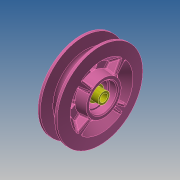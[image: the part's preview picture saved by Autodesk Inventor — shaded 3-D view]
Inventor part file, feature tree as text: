
AUTODESK INVENTOR PART (.ipt)
format: ipt  version: 2017 (Build 210142000, 142)  size: 988,160 bytes
history: native  units: mm
features: sketch x5, revolve x4, extrude x3, other x2, chamfer x2, plane x2, fillet x1, pattern_circular x1, projected_geometry x1
ambient origin geometry x8: Origin, YZ Plane, XZ Plane, XY Plane, X Axis, Y Axis, Z Axis, Center Point
bodies: Body1 (feature_tree), Body2 (feature_tree)
feature tree (21):
  other  "Sólido1"
  sketch  "Boceto1"  dims[d0=8.0mm d1=28.5mm]
  revolve  "Revolución1"  [1 undecoded]
  sketch  "Boceto2"  dims[d2=24.5mm d3=6.0mm]
  extrude  "Extrusión1"  Depth=6.0mm
  chamfer  "Chaflán1"  Distance=20.0mm
  extrude  "Extrusión2"  Depth=1.0mm
  extrude  "Extrusión3"  Depth=8.0mm
  chamfer  "Chaflán2"  Distance=3.0mm
  plane  "Plano de trabajo1"
  revolve  "Revolución3"  [1 undecoded]
  fillet  "Empalme1"  Radius=48.0mm
  plane  "Plano de trabajo2"
  revolve  "Revolución4"  [1 undecoded]
  pattern_circular  "Patrón circular1"  [2 undecoded]
  revolve  "Revolución2"  [1 undecoded]
  other  "espaciador"
  sketch  "Boceto3"  dims[d4=4.0mm]
  sketch  "Boceto4"  dims[d5=90.0mm d6=20.0mm d7=2.5mm]
  sketch  "Boceto5"  dims[d8=90.0deg d9=60.0mm d10=8.0mm d11=3.0mm d12=2.75mm d13=48.0mm d14=10.0mm d15=0.0mm d16=10.0mm d17=0.0mm d18=6.5mm d20=2.094395mm d21=60.0mm d22=4.0mm d23=3.0mm d24=45.0mm d25=45.0mm d26=8.0mm d27=12.0mm d28=16.0mm d29=8.0mm d30=90.0deg d31=20.0mm d32=30.0mm d33=19.0mm d34=6.368574mm d35=3.0mm d36=0.0mm d37=45.0deg d38=2.094395mm d39=1.5mm d40=40.0mm d41=360.0deg d43=22.5deg d44=2.0mm d45=2.094395mm d46=1.0mm d47=2.0mm d48=45.0deg d49=0.4mm d50=2.0mm d51=45.0deg]
  projected_geometry  "Contorno proyectado1"
note: 6 required parameter values undecoded (feature->parameter linkage not recoverable at this tier; creation-order binding heuristic only, values carry confidence <= 0.55)